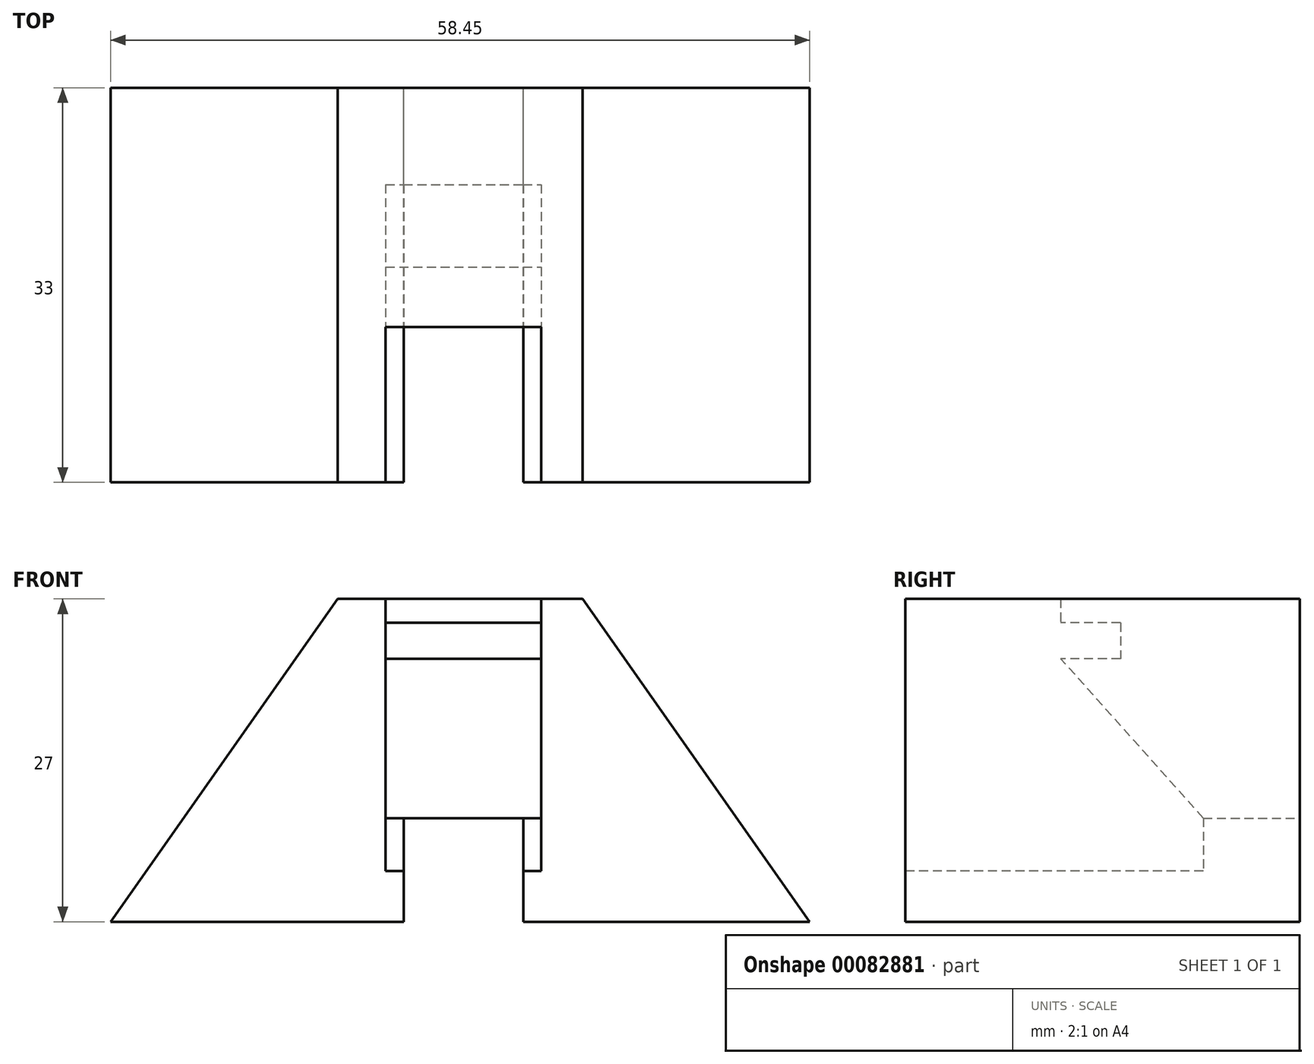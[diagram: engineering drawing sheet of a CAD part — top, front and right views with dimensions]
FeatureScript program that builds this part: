
annotation { "Feature Type Name" : "Feature", "Feature Type Description" : "" }
export const myFeature = defineFeature(function(context is Context, id is Id, definition is map)
    precondition{}
    {
        {
            var Q0;
            Q0=qCreatedBy(makeId("Front.planeOp"),FACE);
            var sketch = newSketch(context, id + "F0", { "sketchPlane" : qUnion([Q0])});
            skLineSegment(sketch, "E0", {"start": v(-29.5, 0) * mm, "end": v(-5, 0) * mm});
            skLineSegment(sketch, "E1", {"start": v(28.95, 0) * mm, "end": v(9.97, 27) * mm});
            skLineSegment(sketch, "E2", {"start": v(9.97, 27) * mm, "end": v(-10.53, 27) * mm});
            skLineSegment(sketch, "E3", {"start": v(-10.53, 27) * mm, "end": v(-29.5, 0) * mm});
            skLineSegment(sketch, "E4.top", {"start": v(-5, 8.67) * mm, "end": v(5, 8.67) * mm});
            skLineSegment(sketch, "E4.left", {"start": v(-5, 0) * mm, "end": v(-5, 8.67) * mm});
            skLineSegment(sketch, "E4.right", {"start": v(5, 0) * mm, "end": v(5, 8.67) * mm});
            skLineSegment(sketch, "E5.trimOffspring", {"start": v(5, 0) * mm, "end": v(28.95, 0) * mm});
            skSolve(sketch);
        }
        {
            var Q0;
            Q0=qSketchRegion(id+"F0",true);
            extrude(context, id + "F1", {"entities" : qUnion([Q0]), "depth" : 33 * mm});
        }
        {
            var Q0;
            Q0=makeQuery(id+"F1.opExtrude","CAP_FACE",FACE,{"disambiguationData":[OSD([sQuery(id+"F0.wireOp",EDGE,"E0"),sQuery(id+"F0.wireOp",EDGE,"E1"),sQuery(id+"F0.wireOp",EDGE,"E2"),sQuery(id+"F0.wireOp",EDGE,"E3"),sQuery(id+"F0.wireOp",EDGE,"E4.top"),sQuery(id+"F0.wireOp",EDGE,"E4.left"),sQuery(id+"F0.wireOp",EDGE,"E4.right"),sQuery(id+"F0.wireOp",EDGE,"E5.trimOffspring")])],"isStart":false});
            var sketch = newSketch(context, id + "F2", { "sketchPlane" : qUnion([Q0])});
            skLineSegment(sketch, "E6.bottom", {"start": v(-6.5, 27) * mm, "end": v(6.5, 27) * mm});
            skLineSegment(sketch, "E6.top", {"start": v(-6.5, 4.25) * mm, "end": v(6.5, 4.25) * mm});
            skLineSegment(sketch, "E6.left", {"start": v(-6.5, 27) * mm, "end": v(-6.5, 4.25) * mm});
            skLineSegment(sketch, "E6.right", {"start": v(6.5, 27) * mm, "end": v(6.5, 4.25) * mm});
            skSolve(sketch);
        }
        {
            var Q0;
            Q0=qSketchRegion(id+"F2",true);
            extrude(context, id + "F3", {"entities" : qUnion([Q0]), "operationType" : NewBodyOperationType.REMOVE, "oppositeDirection" : true, "depth" : 13 * mm});
        }
        {
            var Q0;
            Q0=makeQuery(id+"F3.boolean.opBoolean","COPY",FACE,{"derivedFrom":makeQuery(id+"F3.opExtrude","CAP_FACE",FACE,{"disambiguationData":[OSD([sQuery(id+"F2.wireOp",EDGE,"E6.bottom"),sQuery(id+"F2.wireOp",EDGE,"E6.top"),sQuery(id+"F2.wireOp",EDGE,"E6.left"),sQuery(id+"F2.wireOp",EDGE,"E6.right")])],"isStart":false})});
            var sketch = newSketch(context, id + "F4", { "sketchPlane" : qUnion([Q0])});
            skLineSegment(sketch, "E7.bottom", {"start": v(-6.5, 25) * mm, "end": v(6.5, 25) * mm});
            skLineSegment(sketch, "E7.top", {"start": v(-6.5, 22) * mm, "end": v(6.5, 22) * mm});
            skLineSegment(sketch, "E7.left", {"start": v(-6.5, 25) * mm, "end": v(-6.5, 22) * mm});
            skLineSegment(sketch, "E7.right", {"start": v(6.5, 25) * mm, "end": v(6.5, 22) * mm});
            skSolve(sketch);
        }
        {
            var Q0;
            Q0=qSketchRegion(id+"F4",true);
            extrude(context, id + "F5", {"entities" : qUnion([Q0]), "operationType" : NewBodyOperationType.REMOVE, "oppositeDirection" : true, "depth" : 5 * mm});
        }
        {
            var Q0;
            Q0=qCreatedBy(makeId("Right.planeOp"),FACE);
            var sketch = newSketch(context, id + "F6", { "sketchPlane" : qUnion([Q0])});
            skLineSegment(sketch, "E8", {"start": v(-20, 22) * mm, "end": v(-20, 4.25) * mm});
            skLineSegment(sketch, "E9", {"start": v(-20, 4.25) * mm, "end": v(-8.1, 4.25) * mm});
            skLineSegment(sketch, "E10", {"start": v(-8.09, 4.25) * mm, "end": v(-8.1, 8.67) * mm});
            skLineSegment(sketch, "E11", {"start": v(-8.1, 8.67) * mm, "end": v(-20, 22) * mm});
            skSolve(sketch);
        }
        {
            var Q0;
            Q0=qSketchRegion(id+"F6",true);
            extrude(context, id + "F7", {"entities" : qUnion([Q0]), "operationType" : NewBodyOperationType.REMOVE, "endBound" : BoundingType.SYMMETRIC, "oppositeDirection" : true, "depth" : 13 * mm});
        }
    });
